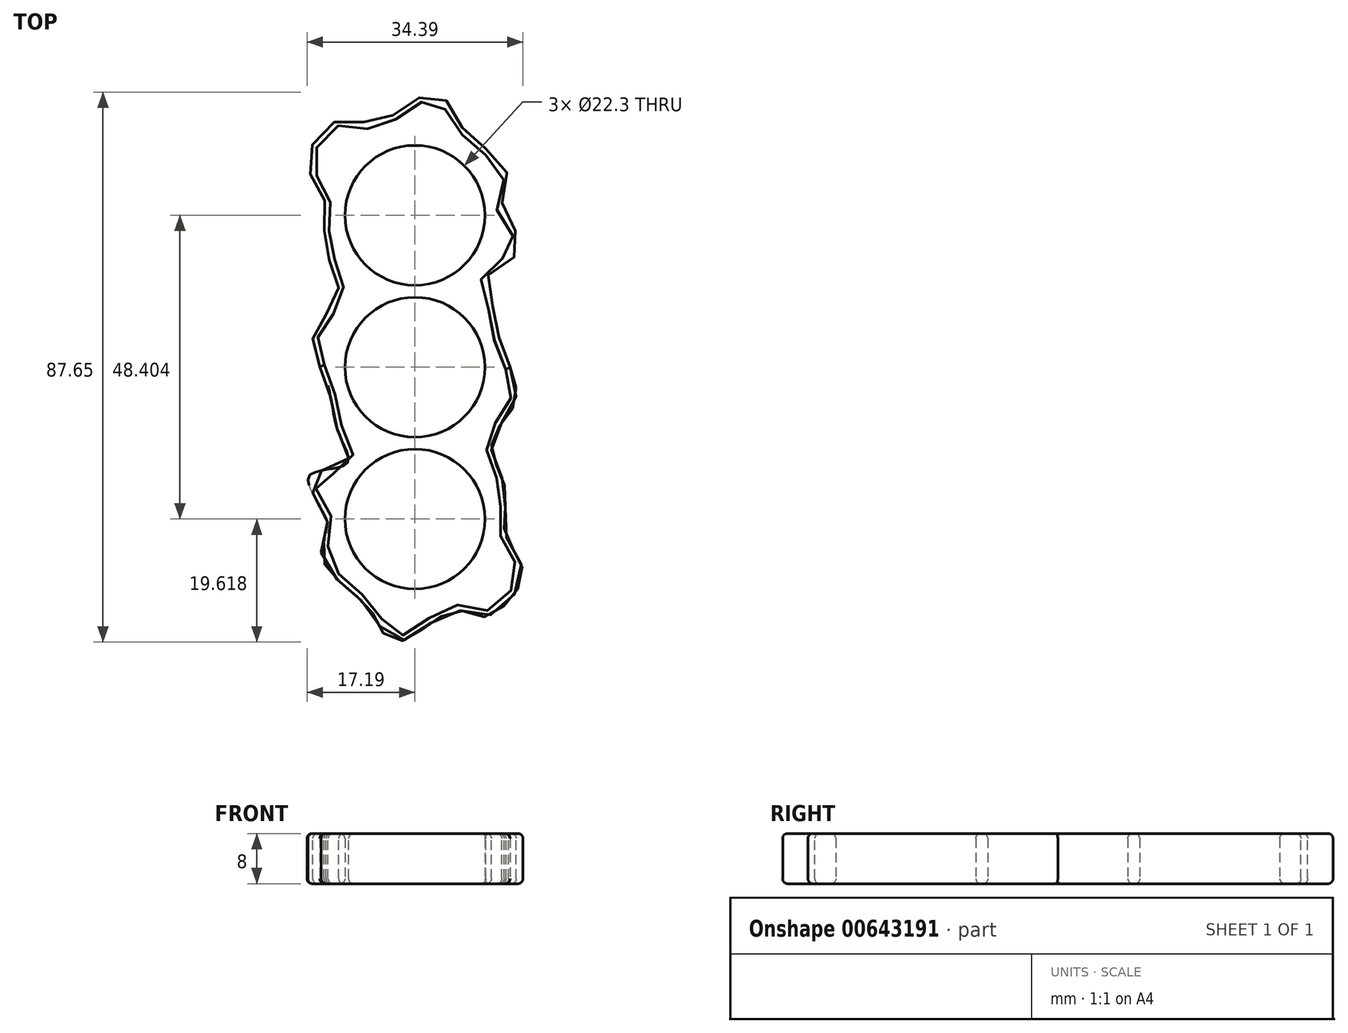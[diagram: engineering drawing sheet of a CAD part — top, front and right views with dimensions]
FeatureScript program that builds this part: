
annotation { "Feature Type Name" : "Feature", "Feature Type Description" : "" }
export const myFeature = defineFeature(function(context is Context, id is Id, definition is map)
    precondition{}
    {
        {
            var Q0;
            Q0=qCreatedBy(makeId("Top.planeOp"),FACE);
            var sketch = newSketch(context, id + "F0", { "sketchPlane" : qUnion([Q0])});
            skCircle(sketch, "E0", {"center": v(0, 0) * mm, "radius": 11.15 * mm});
            skCircle(sketch, "E1", {"center": v(0, 24.2) * mm, "radius": 11.15 * mm});
            skCircle(sketch, "E2.MirrorC", {"center": v(0, -24.2) * mm, "radius": 11.15 * mm});
            skFitSpline(sketch, "E3", {"points": [v(15.16, 0) * mm, v(14.17, -8.4) * mm, v(12.16, -12.92) * mm, v(14.42, -19.69) * mm, v(14.42, -26.7) * mm, v(17.18, -32.98) * mm, v(11.16, -39.75) * mm, v(7.15, -38.75) * mm, v(2.63, -40.75) * mm, v(-3.64, -43.76) * mm, v(-6.4, -39.75) * mm, v(-11.66, -34.48) * mm, v(-14.92, -29.72) * mm, v(-13.92, -24.7) * mm, v(-16.93, -17.43) * mm, v(-10.9, -15.42) * mm, v(-12.3, -10.07) * mm, v(-15.16, 0) * mm], "startDerivative": vector(92.18, -223.65) * mm, "endDerivative": vector(-81.2, 120.35) * mm});
            skLineSegment(sketch, "E4", {"start": v(-35.99, 44.27) * mm, "end": v(38.25, 44.27) * mm, "construction": true});
            skFitSpline(sketch, "E5.MirrorCS", {"points": [v(-15.16, 0) * mm, v(-14.17, 8.4) * mm, v(-12.16, 12.92) * mm, v(-14.42, 19.69) * mm, v(-14.42, 26.7) * mm, v(-17.18, 32.98) * mm, v(-11.16, 39.75) * mm, v(-7.15, 38.75) * mm, v(-2.63, 40.75) * mm, v(3.64, 43.76) * mm, v(6.4, 39.75) * mm, v(11.66, 34.48) * mm, v(14.92, 29.72) * mm, v(13.92, 24.7) * mm, v(17.18, 19.19) * mm, v(11.66, 14.67) * mm, v(12.3, 10.07) * mm, v(15.16, 0) * mm], "startDerivative": vector(-103.91, 252) * mm, "endDerivative": vector(81.2, -120.35) * mm});
            skLineSegment(sketch, "E6", {"start": v(-27.96, -43.76) * mm, "end": v(40.25, -43.76) * mm, "construction": true});
            skSolve(sketch);
        }
        {
            var Q0;
            Q0=makeQuery(id+"F0.imprint","IMPRINT",FACE,{"disambiguationData":[TD([[makeQuery(id+"F0.imprint","IMPRINT",EDGE,{"derivedFrom":sQuery(id+"F0.wireOp",EDGE,"E0")}),-1.0]])]});
            extrude(context, id + "F1", {"entities" : qUnion([Q0]), "depth" : 8 * mm, "offsetDistance" : 25 * mm});
        }
        {
            var Q0;
            Q0=makeQuery(id+"F1.opExtrude","CAP_EDGE",EDGE,{"disambiguationData":[OSD([sQuery(id+"F0.wireOp",EDGE,"E2.MirrorC")])],"isStart":false});
            var Q1;
            Q1=makeQuery(id+"F1.opExtrude","CAP_EDGE",EDGE,{"disambiguationData":[OSD([sQuery(id+"F0.wireOp",EDGE,"E0")])],"isStart":false});
            var Q2;
            Q2=makeQuery(id+"F1.opExtrude","CAP_EDGE",EDGE,{"disambiguationData":[OSD([sQuery(id+"F0.wireOp",EDGE,"E1")])],"isStart":false});
            var Q3;
            Q3=makeQuery(id+"F1.opExtrude","CAP_EDGE",EDGE,{"disambiguationData":[OSD([sQuery(id+"F0.wireOp",EDGE,"E0")])],"isStart":true});
            var Q4;
            Q4=makeQuery(id+"F1.opExtrude","CAP_EDGE",EDGE,{"disambiguationData":[OSD([sQuery(id+"F0.wireOp",EDGE,"E2.MirrorC")])],"isStart":true});
            var Q5;
            Q5=makeQuery(id+"F1.opExtrude","CAP_EDGE",EDGE,{"disambiguationData":[OSD([sQuery(id+"F0.wireOp",EDGE,"E1")])],"isStart":true});
            fillet(context, id + "F2", {"entities" : qUnion([Q0, Q1, Q2, Q3, Q4, Q5]), "radius" : 0.8 * mm, "allowEdgeOverflow" : false});
        }
        {
            var Q0;
            Q0=makeQuery(id+"F1.opExtrude","CAP_EDGE",EDGE,{"disambiguationData":[OSD([sQuery(id+"F0.wireOp",EDGE,"E3")])],"isStart":false});
            var Q1;
            Q1=makeQuery(id+"F1.opExtrude","CAP_EDGE",EDGE,{"disambiguationData":[OSD([sQuery(id+"F0.wireOp",EDGE,"E5.MirrorCS")])],"isStart":false});
            var Q2;
            Q2=makeQuery(id+"F1.opExtrude","CAP_EDGE",EDGE,{"disambiguationData":[OSD([sQuery(id+"F0.wireOp",EDGE,"E5.MirrorCS")])],"isStart":true});
            var Q3;
            Q3=makeQuery(id+"F1.opExtrude","CAP_EDGE",EDGE,{"disambiguationData":[OSD([sQuery(id+"F0.wireOp",EDGE,"E3")])],"isStart":true});
            fillet(context, id + "F3", {"entities" : qUnion([Q0, Q1, Q2, Q3]), "radius" : 0.8 * mm, "tangentPropagation" : true, "allowEdgeOverflow" : false});
        }
    });
